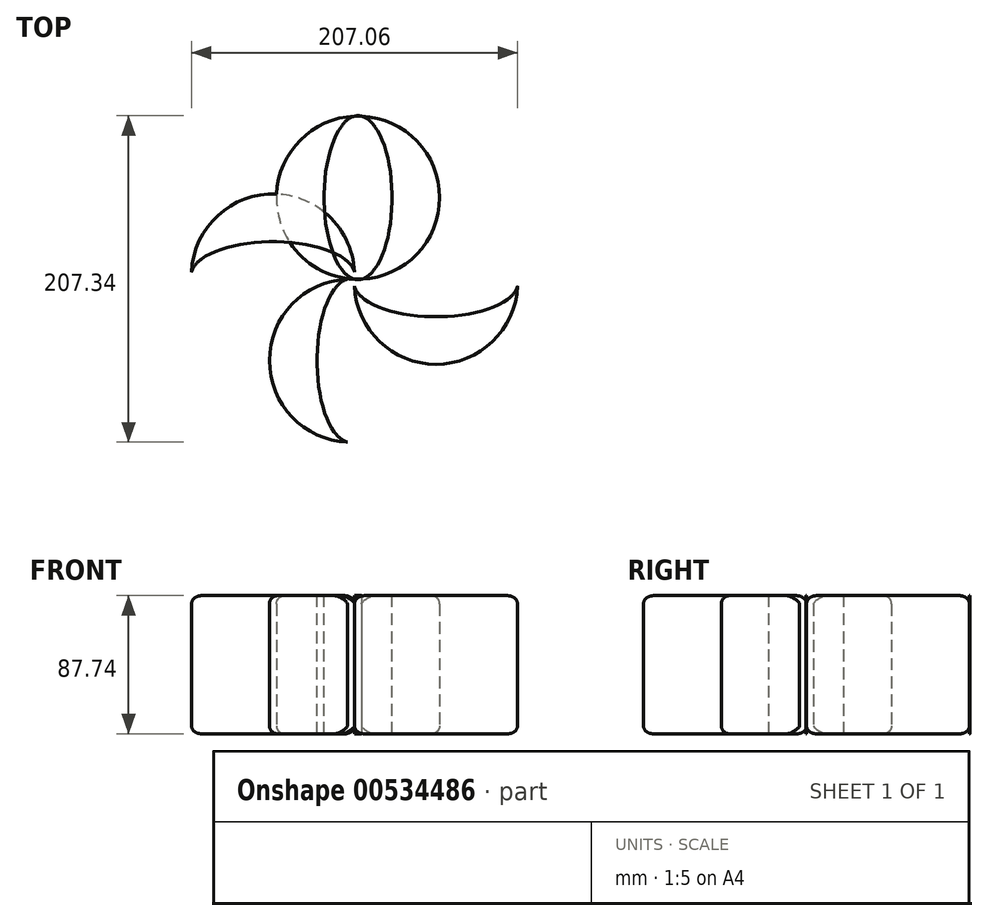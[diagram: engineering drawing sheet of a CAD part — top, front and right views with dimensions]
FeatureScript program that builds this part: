
annotation { "Feature Type Name" : "Feature", "Feature Type Description" : "" }
export const myFeature = defineFeature(function(context is Context, id is Id, definition is map)
    precondition{}
    {
        {
            var Q0;
            Q0=qCreatedBy(makeId("Top.planeOp"),FACE);
            var sketch = newSketch(context, id + "F0", { "sketchPlane" : qUnion([Q0])});
            skCircle(sketch, "E0", {"center": v(0, 0) * mm, "radius": 51.81 * mm});
            skEllipse(sketch, "E1", {"center": v(0, 0) * mm, "majorRadius": 52.05 * mm, "minorRadius": 21.6 * mm, "majorAxis": v(0, -1)});
            skSolve(sketch);
        }
        {
            var Q0;
            {var subQ0=sQuery(id+"F0.wireOp",EDGE,"E1");var subQ1=sQuery(id+"F0.wireOp",EDGE,"E0");var subQ2=makeQuery(id+"F0.imprint","INTERSECT",VERTEX,{"disambiguationData":[OD(2.0)],"derivedFrom":[subQ1,subQ0]});Q0=makeQuery(id+"F0.imprint","IMPRINT",FACE,{"disambiguationData":[TD([[makeQuery(id+"F0.imprint","IMPRINT",EDGE,{"disambiguationData":[TD([[subQ2,-1.0]])],"derivedFrom":subQ1}),-1.0]])]});}
            var Q1;
            {var subQ0=sQuery(id+"F0.wireOp",EDGE,"E1");var subQ1=sQuery(id+"F0.wireOp",EDGE,"E0");var subQ2=makeQuery(id+"F0.imprint","INTERSECT",VERTEX,{"disambiguationData":[OD(0.0)],"derivedFrom":[subQ1,subQ0]});Q1=makeQuery(id+"F0.imprint","IMPRINT",FACE,{"disambiguationData":[TD([[makeQuery(id+"F0.imprint","IMPRINT",EDGE,{"disambiguationData":[TD([[subQ2,1.0]])],"derivedFrom":subQ1}),-1.0]])]});}
            var Q2;
            {var subQ0=sQuery(id+"F0.wireOp",EDGE,"E1");var subQ1=sQuery(id+"F0.wireOp",EDGE,"E0");var subQ2=makeQuery(id+"F0.imprint","INTERSECT",VERTEX,{"disambiguationData":[OD(1.0)],"derivedFrom":[subQ1,subQ0]});Q2=makeQuery(id+"F0.imprint","IMPRINT",FACE,{"disambiguationData":[TD([[makeQuery(id+"F0.imprint","IMPRINT",EDGE,{"disambiguationData":[TD([[subQ2,1.0]])],"derivedFrom":subQ1}),1.0]])]});}
            var Q3;
            {var subQ0=sQuery(id+"F0.wireOp",EDGE,"E1");var subQ1=sQuery(id+"F0.wireOp",EDGE,"E0");var subQ2=makeQuery(id+"F0.imprint","INTERSECT",VERTEX,{"disambiguationData":[OD(0.0)],"derivedFrom":[subQ1,subQ0]});Q3=makeQuery(id+"F0.imprint","IMPRINT",FACE,{"disambiguationData":[TD([[makeQuery(id+"F0.imprint","IMPRINT",EDGE,{"disambiguationData":[TD([[subQ2,-1.0]])],"derivedFrom":subQ1}),1.0]])]});}
            extrude(context, id + "F1", {"entities" : qUnion([Q0, Q1, Q2, Q3]), "depth" : 87.74 * mm, "offsetDistance" : 25.4 * mm});
        }
        {
            var Q0;
            {var subQ0=sQuery(id+"F0.wireOp",EDGE,"E1");var subQ1=sQuery(id+"F0.wireOp",EDGE,"E0");Q0=makeQuery(id+"F1.opExtrude","CAP_EDGE",EDGE,{"disambiguationData":[OSD([subQ1]),TDD([makeQuery(id+"F0.imprint","IMPRINT",EDGE,{"disambiguationData":[TD([[makeQuery(id+"F0.imprint","INTERSECT",VERTEX,{"disambiguationData":[OD(0.0)],"derivedFrom":[subQ1,subQ0]}),-1.0]])],"derivedFrom":subQ1})])],"isStart":false});}
            var Q1;
            {var subQ0=sQuery(id+"F0.wireOp",EDGE,"E1");var subQ1=sQuery(id+"F0.wireOp",EDGE,"E0");Q1=makeQuery(id+"F1.opExtrude","CAP_EDGE",EDGE,{"disambiguationData":[OSD([subQ1]),TDD([makeQuery(id+"F0.imprint","IMPRINT",EDGE,{"disambiguationData":[TD([[makeQuery(id+"F0.imprint","INTERSECT",VERTEX,{"disambiguationData":[OD(1.0)],"derivedFrom":[subQ1,subQ0]}),1.0]])],"derivedFrom":subQ1})])],"isStart":false});}
            fillet(context, id + "F2", {"entities" : qUnion([Q0, Q1]), "radius" : 5.27 * mm, "tangentPropagation" : true, "allowEdgeOverflow" : false});
        }
        {
            var Q0;
            {var subQ0=sQuery(id+"F0.wireOp",EDGE,"E1");var subQ1=sQuery(id+"F0.wireOp",EDGE,"E0");Q0=makeQuery(id+"F1.opExtrude","CAP_EDGE",EDGE,{"disambiguationData":[OSD([subQ1]),TDD([makeQuery(id+"F0.imprint","IMPRINT",EDGE,{"disambiguationData":[TD([[makeQuery(id+"F0.imprint","INTERSECT",VERTEX,{"disambiguationData":[OD(1.0)],"derivedFrom":[subQ1,subQ0]}),1.0]])],"derivedFrom":subQ1})])],"isStart":true});}
            var Q1;
            {var subQ0=sQuery(id+"F0.wireOp",EDGE,"E1");var subQ1=sQuery(id+"F0.wireOp",EDGE,"E0");Q1=makeQuery(id+"F1.opExtrude","CAP_EDGE",EDGE,{"disambiguationData":[OSD([subQ1]),TDD([makeQuery(id+"F0.imprint","IMPRINT",EDGE,{"disambiguationData":[TD([[makeQuery(id+"F0.imprint","INTERSECT",VERTEX,{"disambiguationData":[OD(0.0)],"derivedFrom":[subQ1,subQ0]}),-1.0]])],"derivedFrom":subQ1})])],"isStart":true});}
            fillet(context, id + "F3", {"entities" : qUnion([Q0, Q1]), "radius" : 5.08 * mm, "tangentPropagation" : true, "allowEdgeOverflow" : false});
        }
        {
            var Q0;
            {var subQ0=sQuery(id+"F0.wireOp",EDGE,"E1");var subQ1=sQuery(id+"F0.wireOp",EDGE,"E0");var subQ2=makeQuery(id+"F0.imprint","INTERSECT",VERTEX,{"disambiguationData":[OD(1.0)],"derivedFrom":[subQ1,subQ0]});Q0=makeQuery(id+"F1.opExtrude","SWEPT_BODY",BODY,{"disambiguationData":[OSD([subQ1,subQ0]),TDD([makeQuery(id+"F0.imprint","IMPRINT",EDGE,{"disambiguationData":[TD([[subQ2,1.0]])],"derivedFrom":subQ1}),makeQuery(id+"F0.imprint","IMPRINT",EDGE,{"disambiguationData":[TD([[subQ2,1.0]])],"derivedFrom":subQ0})])]});}
            var Q1;
            {var subQ0=sQuery(id+"F0.wireOp",EDGE,"E1");var subQ1=sQuery(id+"F0.wireOp",EDGE,"E0");Q1=makeQuery(id+"F1.opExtrude","SWEPT_EDGE",EDGE,{"disambiguationData":[OSD([subQ1,subQ0]),TDD([makeQuery(id+"F0.imprint","INTERSECT",VERTEX,{"disambiguationData":[OD(2.0)],"derivedFrom":[subQ1,subQ0]})]),OD(0.0)]});}
            circularPattern(context, id + "F4", {"entities" : qUnion([Q0]), "axis" : qUnion([Q1]), "angle" : 360 * degree, "instanceCount" : 4, "equalSpace" : true});
        }
    });
